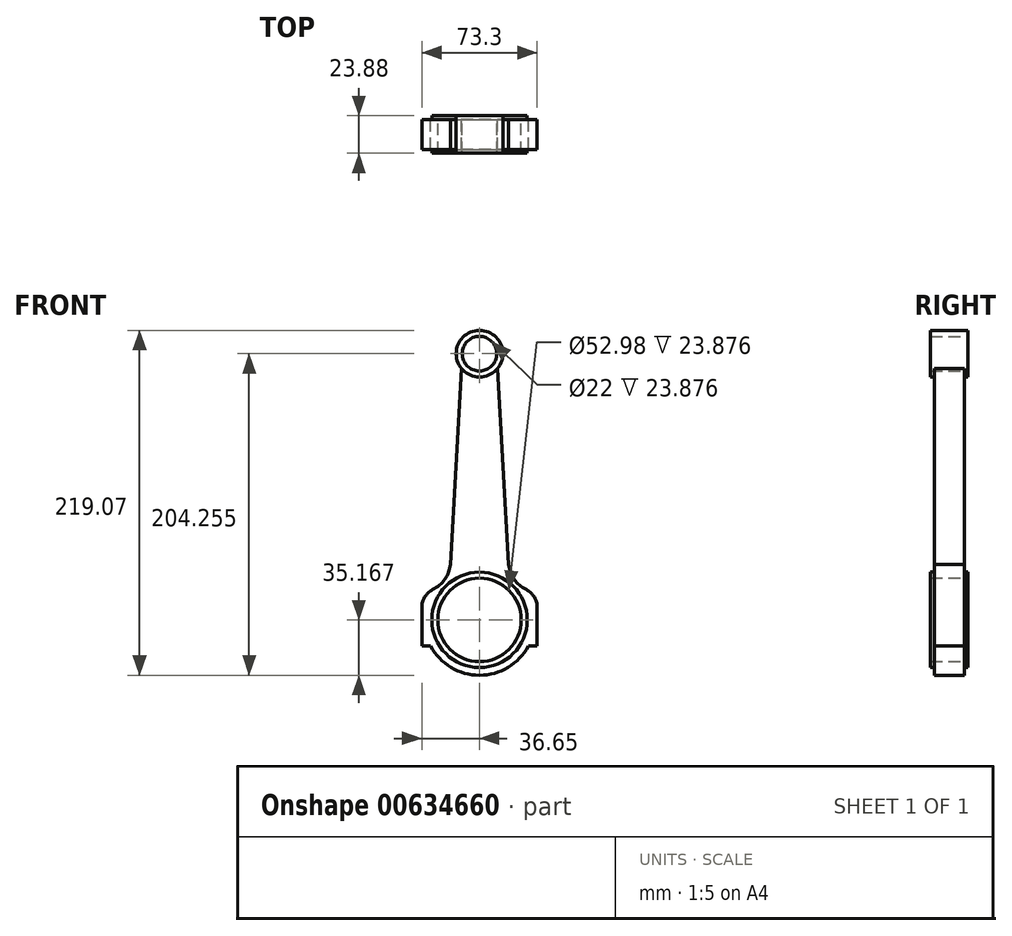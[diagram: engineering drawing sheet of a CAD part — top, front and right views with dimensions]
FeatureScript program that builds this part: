
annotation { "Feature Type Name" : "Feature", "Feature Type Description" : "" }
export const myFeature = defineFeature(function(context is Context, id is Id, definition is map)
    precondition{}
    {
        {
            var Q0;
            Q0=qCreatedBy(makeId("Front.planeOp"),FACE);
            var sketch = newSketch(context, id + "F0", { "sketchPlane" : qUnion([Q0])});
            skCircle(sketch, "E0", {"center": v(0, -25.3) * mm, "radius": 26.5 * mm});
            skLineSegment(sketch, "E1", {"start": v(0, -25.3) * mm, "end": v(0, 143.79) * mm, "construction": true});
            skCircle(sketch, "E2", {"center": v(0, 143.79) * mm, "radius": 11 * mm});
            skCircle(sketch, "E3.0", {"center": v(0, 143.79) * mm, "radius": 14.8 * mm});
            skCircle(sketch, "E4.0", {"center": v(0, -25.3) * mm, "radius": 30.3 * mm});
            skLineSegment(sketch, "E5", {"start": v(0, -25.3) * mm, "end": v(-36.65, -25.3) * mm});
            skLineSegment(sketch, "E6", {"start": v(-36.65, -25.3) * mm, "end": v(-36.65, -17.42) * mm});
            skLineSegment(sketch, "E7", {"start": v(-18.43, 10.03) * mm, "end": v(-10.98, 144.4) * mm});
            skArc(sketch, "E8", {"start": v(-29.7, -6.1) * mm, "mid": v(-22.04, 0.55) * mm, "end": v(-18.43, 10.03) * mm});
            skPoint(sketch, "E8.third.point", {"position": v(-57.8, 21.68) * mm});
            skPoint(sketch, "E9.visualSharp", {"position": v(-36.65, -8.2) * mm});
            skArc(sketch, "E9.filletArc", {"start": v(-29.7, -6.1) * mm, "mid": v(-34.77, -10.78) * mm, "end": v(-36.65, -17.42) * mm});
            skLineSegment(sketch, "E10.MirrorCS", {"start": v(18.43, 10.03) * mm, "end": v(10.98, 144.4) * mm});
            skArc(sketch, "E11.MirrorCS", {"start": v(29.7, -6.1) * mm, "mid": v(22.04, 0.55) * mm, "end": v(18.43, 10.03) * mm});
            skArc(sketch, "E12.MirrorCS", {"start": v(29.7, -6.1) * mm, "mid": v(34.77, -10.78) * mm, "end": v(36.65, -17.42) * mm});
            skLineSegment(sketch, "E13.MirrorCS", {"start": v(36.65, -25.3) * mm, "end": v(36.65, -17.42) * mm});
            skLineSegment(sketch, "E14.MirrorCS", {"start": v(0, -25.3) * mm, "end": v(36.65, -25.3) * mm});
            skLineSegment(sketch, "E15", {"start": v(-36.65, -25.3) * mm, "end": v(-36.65, -41.9) * mm});
            skLineSegment(sketch, "E16", {"start": v(-36.65, -41.9) * mm, "end": v(-31, -41.9) * mm});
            skLineSegment(sketch, "E17.MirrorCS", {"start": v(36.65, -41.9) * mm, "end": v(31, -41.9) * mm});
            skLineSegment(sketch, "E18.MirrorCS", {"start": v(36.65, -25.3) * mm, "end": v(36.65, -41.9) * mm});
            skArc(sketch, "E19", {"start": v(-31, -41.9) * mm, "mid": v(0, -60.47) * mm, "end": v(31, -41.9) * mm});
            skPoint(sketch, "E20.orphan", {"position": v(-25.36, -41.9) * mm});
            skPoint(sketch, "E21.orphan", {"position": v(25.36, -41.9) * mm});
            skSolve(sketch);
        }
        {
            var Q0;
            {var subQ0=sQuery(id+"F0.wireOp",EDGE,"E5");var subQ1=sQuery(id+"F0.wireOp",EDGE,"E0");var subQ2=makeQuery(id+"F0.imprint","INTERSECT",VERTEX,{"derivedFrom":[subQ1,subQ0]});Q0=makeQuery(id+"F0.imprint","IMPRINT",FACE,{"disambiguationData":[TD([[makeQuery(id+"F0.imprint","IMPRINT",EDGE,{"disambiguationData":[TD([[subQ2,1.0]])],"derivedFrom":subQ1}),-1.0]])]});}
            extrude(context, id + "F1", {"entities" : qUnion([Q0]), "depth" : 23.88 * mm, "offsetDistance" : 25.4 * mm, "symmetric" : true});
        }
        {
            var Q0;
            {var subQ0=sQuery(id+"F0.wireOp",EDGE,"E5");var subQ1=sQuery(id+"F0.wireOp",EDGE,"E0");var subQ2=makeQuery(id+"F0.imprint","INTERSECT",VERTEX,{"derivedFrom":[subQ1,subQ0]});Q0=makeQuery(id+"F0.imprint","IMPRINT",FACE,{"disambiguationData":[TD([[makeQuery(id+"F0.imprint","IMPRINT",EDGE,{"disambiguationData":[TD([[subQ2,-1.0]])],"derivedFrom":subQ1}),-1.0]])]});}
            extrude(context, id + "F2", {"entities" : qUnion([Q0]), "depth" : 23.88 * mm, "offsetDistance" : 25.4 * mm, "symmetric" : true});
        }
        {
            var Q0;
            {var subQ12=sQuery(id+"F0.wireOp",EDGE,"E6");Q0=makeQuery(id+"F0.imprint","IMPRINT",FACE,{"disambiguationData":[TD([[makeQuery(id+"F0.imprint","IMPRINT",EDGE,{"derivedFrom":subQ12}),-1.0]])]});}
            extrude(context, id + "F3", {"entities" : qUnion([Q0]), "operationType" : NewBodyOperationType.ADD, "depth" : 19.05 * mm, "offsetDistance" : 25.4 * mm, "symmetric" : true});
        }
        {
            var Q0;
            {var subQ0=sQuery(id+"F0.wireOp",EDGE,"E15");Q0=makeQuery(id+"F0.imprint","IMPRINT",FACE,{"disambiguationData":[TD([[makeQuery(id+"F0.imprint","IMPRINT",EDGE,{"derivedFrom":subQ0}),1.0]])]});}
            extrude(context, id + "F4", {"entities" : qUnion([Q0]), "operationType" : NewBodyOperationType.ADD, "depth" : 19.05 * mm, "offsetDistance" : 25.4 * mm, "symmetric" : true});
        }
        {
            var Q0;
            {var subQ0=sQuery(id+"F0.wireOp",EDGE,"E7");var subQ1=sQuery(id+"F0.wireOp",EDGE,"E2");var subQ2=makeQuery(id+"F0.imprint","INTERSECT",VERTEX,{"derivedFrom":[subQ1,subQ0]});Q0=makeQuery(id+"F0.imprint","IMPRINT",FACE,{"disambiguationData":[TD([[makeQuery(id+"F0.imprint","IMPRINT",EDGE,{"disambiguationData":[TD([[subQ2,1.0]])],"derivedFrom":subQ1}),-1.0]])]});}
            var Q1;
            {var subQ0=sQuery(id+"F0.wireOp",EDGE,"E7");var subQ1=sQuery(id+"F0.wireOp",EDGE,"E2");var subQ2=makeQuery(id+"F0.imprint","INTERSECT",VERTEX,{"derivedFrom":[subQ1,subQ0]});Q1=makeQuery(id+"F0.imprint","IMPRINT",FACE,{"disambiguationData":[TD([[makeQuery(id+"F0.imprint","IMPRINT",EDGE,{"disambiguationData":[TD([[subQ2,-1.0]])],"derivedFrom":subQ1}),-1.0]])]});}
            extrude(context, id + "F5", {"entities" : qUnion([Q0, Q1]), "operationType" : NewBodyOperationType.ADD, "depth" : 23.88 * mm, "offsetDistance" : 25.4 * mm, "symmetric" : true});
        }
    });
